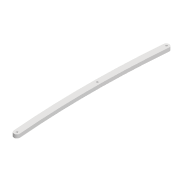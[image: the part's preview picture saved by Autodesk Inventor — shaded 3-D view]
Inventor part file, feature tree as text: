
AUTODESK INVENTOR PART (.ipt)
format: ipt  version: 2022 (Build 260153000, 153)  size: 97,280 bytes
history: native  units: mm
features: extrude x1
ambient origin geometry x8: Origin, YZ Plane, XZ Plane, XY Plane, X Axis, Y Axis, Z Axis, Center Point
bodies: Solid1 (feature_tree)
feature tree (1):
  extrude  "Extrusion1"  Depth=3.3mm
